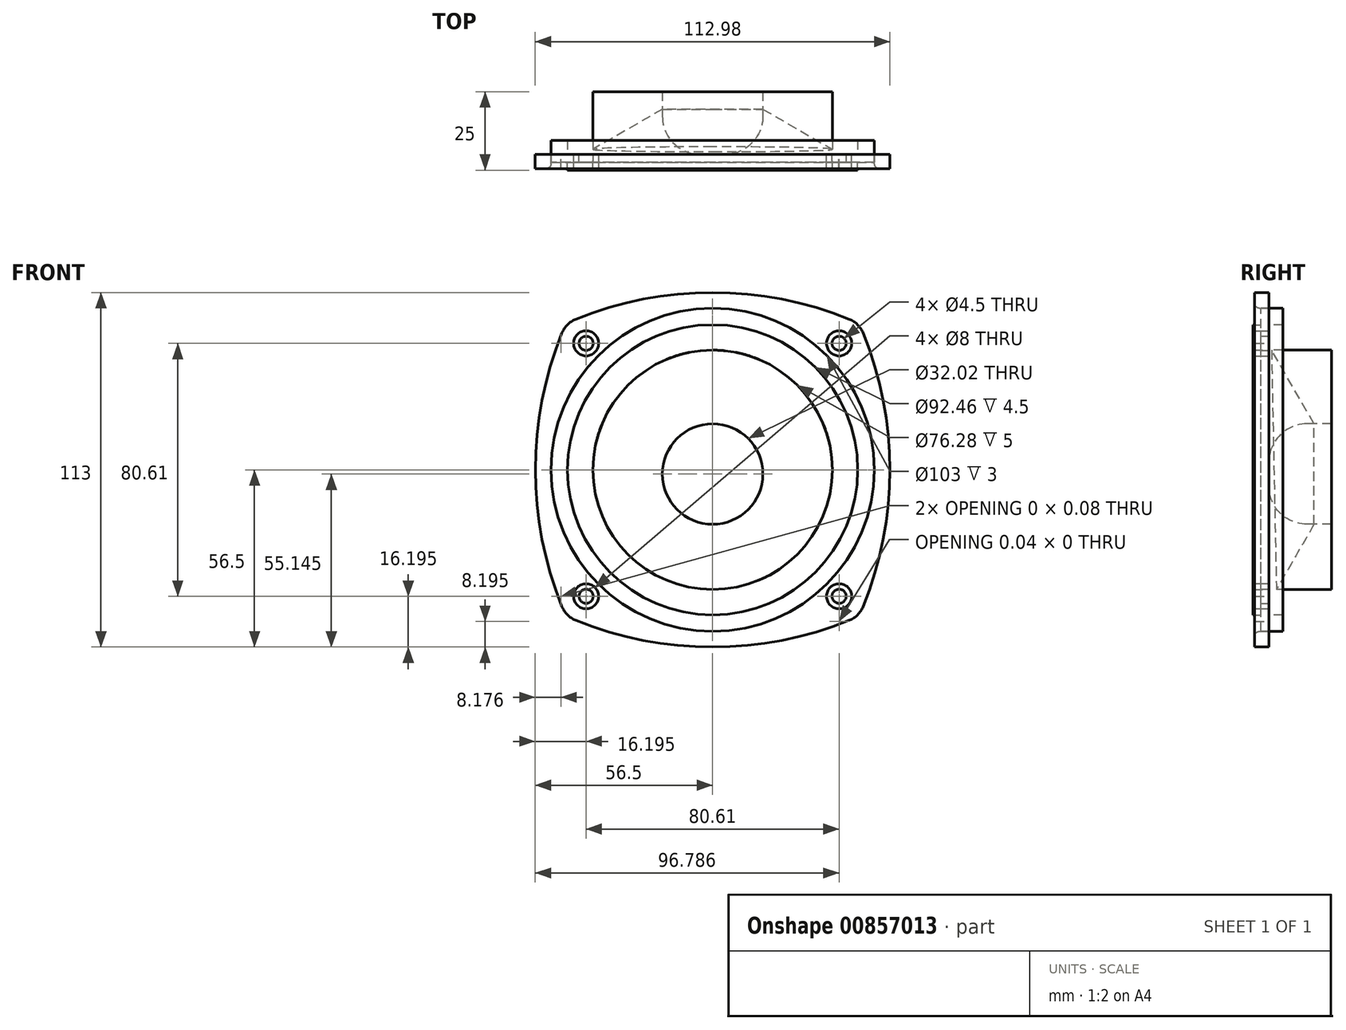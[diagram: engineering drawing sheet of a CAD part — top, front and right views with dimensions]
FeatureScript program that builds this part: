
annotation { "Feature Type Name" : "Feature", "Feature Type Description" : "" }
export const myFeature = defineFeature(function(context is Context, id is Id, definition is map)
    precondition{}
    {
        {
            var Q0;
            Q0=qCreatedBy(makeId("Front.planeOp"),FACE);
            var sketch = newSketch(context, id + "F0", { "sketchPlane" : qUnion([Q0])});
            skCircle(sketch, "E0", {"center": v(0, 0) * mm, "radius": 51.5 * mm});
            skPoint(sketch, "E1", {"position": v(56.5, 0) * mm});
            skPoint(sketch, "E2", {"position": v(-56.5, 0) * mm});
            skPoint(sketch, "E3", {"position": v(43.13, 43.13) * mm});
            skPoint(sketch, "E4", {"position": v(40.3, 40.3) * mm});
            skCircle(sketch, "E5", {"center": v(40.3, 40.3) * mm, "radius": 4 * mm});
            skCircle(sketch, "E6", {"center": v(40.3, 40.3) * mm, "radius": 2.25 * mm});
            skCircle(sketch, "E7.1.0", {"center": v(-40.3, 40.3) * mm, "radius": 4 * mm});
            skCircle(sketch, "E7.1.1", {"center": v(-40.3, 40.3) * mm, "radius": 2.25 * mm});
            skCircle(sketch, "E7.2.0", {"center": v(-40.3, -40.3) * mm, "radius": 4 * mm});
            skCircle(sketch, "E7.2.1", {"center": v(-40.3, -40.3) * mm, "radius": 2.25 * mm});
            skCircle(sketch, "E7.3.0", {"center": v(40.3, -40.3) * mm, "radius": 4 * mm});
            skCircle(sketch, "E7.3.1", {"center": v(40.3, -40.3) * mm, "radius": 2.25 * mm});
            skLineSegment(sketch, "E8", {"start": v(-48.32, 40.34) * mm, "end": v(-48.32, 40.27) * mm});
            skFitSpline(sketch, "E9", {"points": [v(-40.29, -48.3) * mm, v(0, -56.5) * mm, v(40.3, -48.3) * mm], "startDerivative": vector(80.54, -24.59) * mm, "endDerivative": vector(80.6, 24.58) * mm});
            skLineSegment(sketch, "E10.trimOffspring", {"start": v(-48.32, -40.27) * mm, "end": v(-48.32, -40.34) * mm});
            skArc(sketch, "E11.trimOffspring", {"start": v(-48.32, -40.27) * mm, "mid": v(-48.32, -40.3) * mm, "end": v(-48.32, -40.34) * mm});
            skArc(sketch, "E12.1.0", {"start": v(40.27, -48.3) * mm, "mid": v(40.29, -48.3) * mm, "end": v(40.3, -48.3) * mm});
            skArc(sketch, "E12.3.0", {"start": v(-48.32, 40.34) * mm, "mid": v(-48.32, 40.3) * mm, "end": v(-48.32, 40.27) * mm});
            skPoint(sketch, "E13.orphan", {"position": v(-45.98, 45.96) * mm});
            skLineSegment(sketch, "E14.trimOffspring", {"start": v(40.27, -48.3) * mm, "end": v(40.3, -48.3) * mm});
            skPoint(sketch, "E15.orphan", {"position": v(0, -1.36) * mm});
            skPoint(sketch, "E16.orphan", {"position": v(-45.96, -45.96) * mm});
            skPoint(sketch, "E17.start.orphan", {"position": v(45.94, -45.96) * mm});
            skPoint(sketch, "E18.orphan", {"position": v(45.96, 45.96) * mm});
            skCircle(sketch, "E19", {"center": v(0, 0) * mm, "radius": 46.23 * mm});
            skCircle(sketch, "E20", {"center": v(0, 0) * mm, "radius": 38.14 * mm});
            skCircle(sketch, "E21", {"center": v(0, -1.36) * mm, "radius": 16 * mm});
            skLineSegment(sketch, "E22", {"start": v(-45.98, 45.96) * mm, "end": v(45.94, -45.96) * mm});
            skLineSegment(sketch, "E23", {"start": v(-45.98, 45.96) * mm, "end": v(-46.69, 46.67) * mm});
            skPoint(sketch, "E24", {"position": v(-46.69, 46.67) * mm});
            skPoint(sketch, "E25.1.0", {"position": v(-46.69, -46.67) * mm});
            skPoint(sketch, "E25.2.0", {"position": v(46.65, -46.67) * mm});
            skPoint(sketch, "E25.3.0", {"position": v(46.65, 46.67) * mm});
            skPoint(sketch, "E25.center", {"position": v(-0.02, 0) * mm});
            skPoint(sketch, "E26.1.internal.orphan", {"position": v(-0.02, 56.5) * mm});
            skArc(sketch, "E27", {"start": v(46.65, 46.67) * mm, "mid": v(-0.02, 56.5) * mm, "end": v(-46.69, 46.67) * mm});
            skArc(sketch, "E28.1.0", {"start": v(46.65, -46.67) * mm, "mid": v(56.48, 0) * mm, "end": v(46.65, 46.67) * mm});
            skArc(sketch, "E28.2.0", {"start": v(-46.69, -46.67) * mm, "mid": v(-0.02, -56.5) * mm, "end": v(46.65, -46.67) * mm});
            skLineSegment(sketch, "E28.anchor1", {"start": v(-0.02, 0) * mm, "end": v(-0.02, -59.19) * mm, "construction": true});
            skLineSegment(sketch, "E28.anchor2", {"start": v(-0.02, 0) * mm, "end": v(-0.02, 59.19) * mm, "construction": true});
            skArc(sketch, "E29", {"start": v(-46.69, 46.67) * mm, "mid": v(-56.5, 0) * mm, "end": v(-46.69, -46.67) * mm});
            skSolve(sketch);
        }
        {
            var Q0;
            Q0=makeQuery(id+"F0.imprint","IMPRINT",FACE,{"disambiguationData":[TD([[makeQuery(id+"F0.imprint","IMPRINT",EDGE,{"derivedFrom":sQuery(id+"F0.wireOp",EDGE,"E0")}),-1.0]])]});
            extrude(context, id + "F1", {"entities" : qUnion([Q0]), "depth" : 4.5 * mm, "offsetDistance" : 25 * mm});
        }
        {
            var Q0;
            Q0=makeQuery(id+"F1.opExtrude","CAP_EDGE",EDGE,{"disambiguationData":[OSD([sQuery(id+"F0.wireOp",EDGE,"E0")])],"isStart":false});
            fillet(context, id + "F2", {"entities" : qUnion([Q0]), "radius" : 1.5 * mm, "tangentPropagation" : true, "allowEdgeOverflow" : false});
        }
        {
            var Q0;
            Q0=makeQuery(id+"F0.imprint","IMPRINT",FACE,{"disambiguationData":[TD([[makeQuery(id+"F0.imprint","IMPRINT",EDGE,{"derivedFrom":sQuery(id+"F0.wireOp",EDGE,"E0")}),1.0]])]});
            extrude(context, id + "F3", {"entities" : qUnion([Q0]), "oppositeDirection" : true, "depth" : 4.5 * mm, "offsetDistance" : 25 * mm});
        }
        {
            var Q0;
            Q0=makeQuery(id+"F0.imprint","IMPRINT",FACE,{"disambiguationData":[TD([[makeQuery(id+"F0.imprint","IMPRINT",EDGE,{"derivedFrom":sQuery(id+"F0.wireOp",EDGE,"E0")}),1.0]])]});
            extrude(context, id + "F4", {"entities" : qUnion([Q0]), "depth" : 2.5 * mm, "offsetDistance" : 25 * mm});
        }
        {
            var Q0;
            Q0=makeQuery(id+"F0.imprint","IMPRINT",FACE,{"disambiguationData":[TD([[makeQuery(id+"F0.imprint","IMPRINT",EDGE,{"derivedFrom":sQuery(id+"F0.wireOp",EDGE,"E19")}),1.0]])]});
            extrude(context, id + "F5", {"entities" : qUnion([Q0]), "operationType" : NewBodyOperationType.ADD, "depth" : 5 * mm, "offsetDistance" : 25 * mm});
        }
        {
            var Q0;
            Q0=makeQuery(id+"F0.imprint","IMPRINT",FACE,{"disambiguationData":[TD([[makeQuery(id+"F0.imprint","IMPRINT",EDGE,{"derivedFrom":sQuery(id+"F0.wireOp",EDGE,"E20")}),1.0]])]});
            extrude(context, id + "F6", {"entities" : qUnion([Q0]), "oppositeDirection" : true, "depth" : 20 * mm, "offsetDistance" : 25 * mm});
        }
        {
            var Q0;
            Q0=makeQuery(id+"F6.opExtrude","CAP_EDGE",EDGE,{"disambiguationData":[OSD([sQuery(id+"F0.wireOp",EDGE,"E21")])],"isStart":true});
            chamfer(context, id + "F7", {"entities" : qUnion([Q0]), "chamferType" : ChamferType.OFFSET_ANGLE, "width" : 25 * mm, "oppositeDirection" : true, "angle" : 30 * degree});
        }
        {
            var Q0;
            Q0=makeQuery(id+"F0.imprint","IMPRINT",FACE,{"disambiguationData":[TD([[makeQuery(id+"F0.imprint","IMPRINT",EDGE,{"derivedFrom":sQuery(id+"F0.wireOp",EDGE,"E21")}),1.0]])]});
            extrude(context, id + "F8", {"entities" : qUnion([Q0]), "oppositeDirection" : true, "depth" : 20 * mm, "offsetDistance" : 25 * mm});
        }
        {
            var Q0;
            {var subQ0=sQuery(id+"F0.wireOp",EDGE,"E22");var subQ1=sQuery(id+"F0.wireOp",EDGE,"E7.1.0");var subQ2=makeQuery(id+"F0.imprint","INTERSECT",VERTEX,{"disambiguationData":[OD(0.0)],"derivedFrom":[subQ1,subQ0]});Q0=makeQuery(id+"F0.imprint","IMPRINT",FACE,{"disambiguationData":[TD([[makeQuery(id+"F0.imprint","IMPRINT",EDGE,{"disambiguationData":[TD([[subQ2,-1.0]])],"derivedFrom":subQ1}),1.0]])]});}
            var Q1;
            {var subQ0=sQuery(id+"F0.wireOp",EDGE,"E22");var subQ1=sQuery(id+"F0.wireOp",EDGE,"E7.1.0");var subQ2=makeQuery(id+"F0.imprint","INTERSECT",VERTEX,{"disambiguationData":[OD(0.0)],"derivedFrom":[subQ1,subQ0]});Q1=makeQuery(id+"F0.imprint","IMPRINT",FACE,{"disambiguationData":[TD([[makeQuery(id+"F0.imprint","IMPRINT",EDGE,{"disambiguationData":[TD([[subQ2,1.0]])],"derivedFrom":subQ1}),1.0]])]});}
            var Q2;
            Q2=makeQuery(id+"F0.imprint","IMPRINT",FACE,{"disambiguationData":[TD([[makeQuery(id+"F0.imprint","IMPRINT",EDGE,{"derivedFrom":sQuery(id+"F0.wireOp",EDGE,"E5")}),1.0]])]});
            var Q3;
            Q3=makeQuery(id+"F0.imprint","IMPRINT",FACE,{"disambiguationData":[TD([[makeQuery(id+"F0.imprint","IMPRINT",EDGE,{"derivedFrom":sQuery(id+"F0.wireOp",EDGE,"E7.2.0")}),1.0]])]});
            var Q4;
            {var subQ0=sQuery(id+"F0.wireOp",EDGE,"E22");var subQ1=sQuery(id+"F0.wireOp",EDGE,"E7.3.0");var subQ2=makeQuery(id+"F0.imprint","INTERSECT",VERTEX,{"disambiguationData":[OD(0.0)],"derivedFrom":[subQ1,subQ0]});Q4=makeQuery(id+"F0.imprint","IMPRINT",FACE,{"disambiguationData":[TD([[makeQuery(id+"F0.imprint","IMPRINT",EDGE,{"disambiguationData":[TD([[subQ2,-1.0]])],"derivedFrom":subQ1}),1.0]])]});}
            var Q5;
            {var subQ0=sQuery(id+"F0.wireOp",EDGE,"E22");var subQ1=sQuery(id+"F0.wireOp",EDGE,"E7.3.0");var subQ2=makeQuery(id+"F0.imprint","INTERSECT",VERTEX,{"disambiguationData":[OD(0.0)],"derivedFrom":[subQ1,subQ0]});Q5=makeQuery(id+"F0.imprint","IMPRINT",FACE,{"disambiguationData":[TD([[makeQuery(id+"F0.imprint","IMPRINT",EDGE,{"disambiguationData":[TD([[subQ2,1.0]])],"derivedFrom":subQ1}),1.0]])]});}
            extrude(context, id + "F9", {"entities" : qUnion([Q0, Q1, Q2, Q3, Q4, Q5]), "depth" : 2.5 * mm, "offsetDistance" : 25 * mm});
        }
        {
            var Q0;
            Q0=makeQuery(id+"F8.opExtrude","CAP_EDGE",EDGE,{"disambiguationData":[OSD([sQuery(id+"F0.wireOp",EDGE,"E21")])],"isStart":true});
            fillet(context, id + "F10", {"entities" : qUnion([Q0]), "radius" : 12.2 * mm, "tangentPropagation" : true, "allowEdgeOverflow" : false});
        }
        {
            var Q0;
            Q0=makeQuery(id+"F1.opExtrude","SWEPT_EDGE",EDGE,{"disambiguationData":[OSD([sQuery(id+"F0.wireOp",EDGE,"E27"),sQuery(id+"F0.wireOp",EDGE,"E29")])]});
            var Q1;
            Q1=makeQuery(id+"F1.opExtrude","SWEPT_EDGE",EDGE,{"disambiguationData":[OSD([sQuery(id+"F0.wireOp",EDGE,"E27"),sQuery(id+"F0.wireOp",EDGE,"E28.1.0")])]});
            var Q2;
            Q2=makeQuery(id+"F1.opExtrude","SWEPT_EDGE",EDGE,{"disambiguationData":[OSD([sQuery(id+"F0.wireOp",EDGE,"E28.1.0"),sQuery(id+"F0.wireOp",EDGE,"E28.2.0")])]});
            var Q3;
            Q3=makeQuery(id+"F1.opExtrude","SWEPT_EDGE",EDGE,{"disambiguationData":[OSD([sQuery(id+"F0.wireOp",EDGE,"E28.2.0"),sQuery(id+"F0.wireOp",EDGE,"E29")])]});
            fillet(context, id + "F11", {"entities" : qUnion([Q0, Q1, Q2, Q3]), "radius" : 8 * mm, "allowEdgeOverflow" : false});
        }
    });
